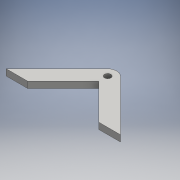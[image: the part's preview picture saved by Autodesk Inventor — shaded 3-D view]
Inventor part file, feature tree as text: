
AUTODESK INVENTOR PART (.ipt)
format: ipt  version: 2016 (Build 200138000, 138)  size: 99,328 bytes
history: native  units: mm
features: extrude x1, sketch x1
ambient origin geometry x8: Origin, YZ Plane, XZ Plane, XY Plane, X Axis, Y Axis, Z Axis, Center Point
bodies: Solid1 (feature_tree)
feature tree (2):
  extrude  "Extrusion1"  Depth=35.0mm
  sketch  "Sketch1"  dims[d0=5.0mm d1=35.0mm d4=45.0mm d5=45.0deg d6=45.0deg d9=5.0mm d10=0.0mm]
